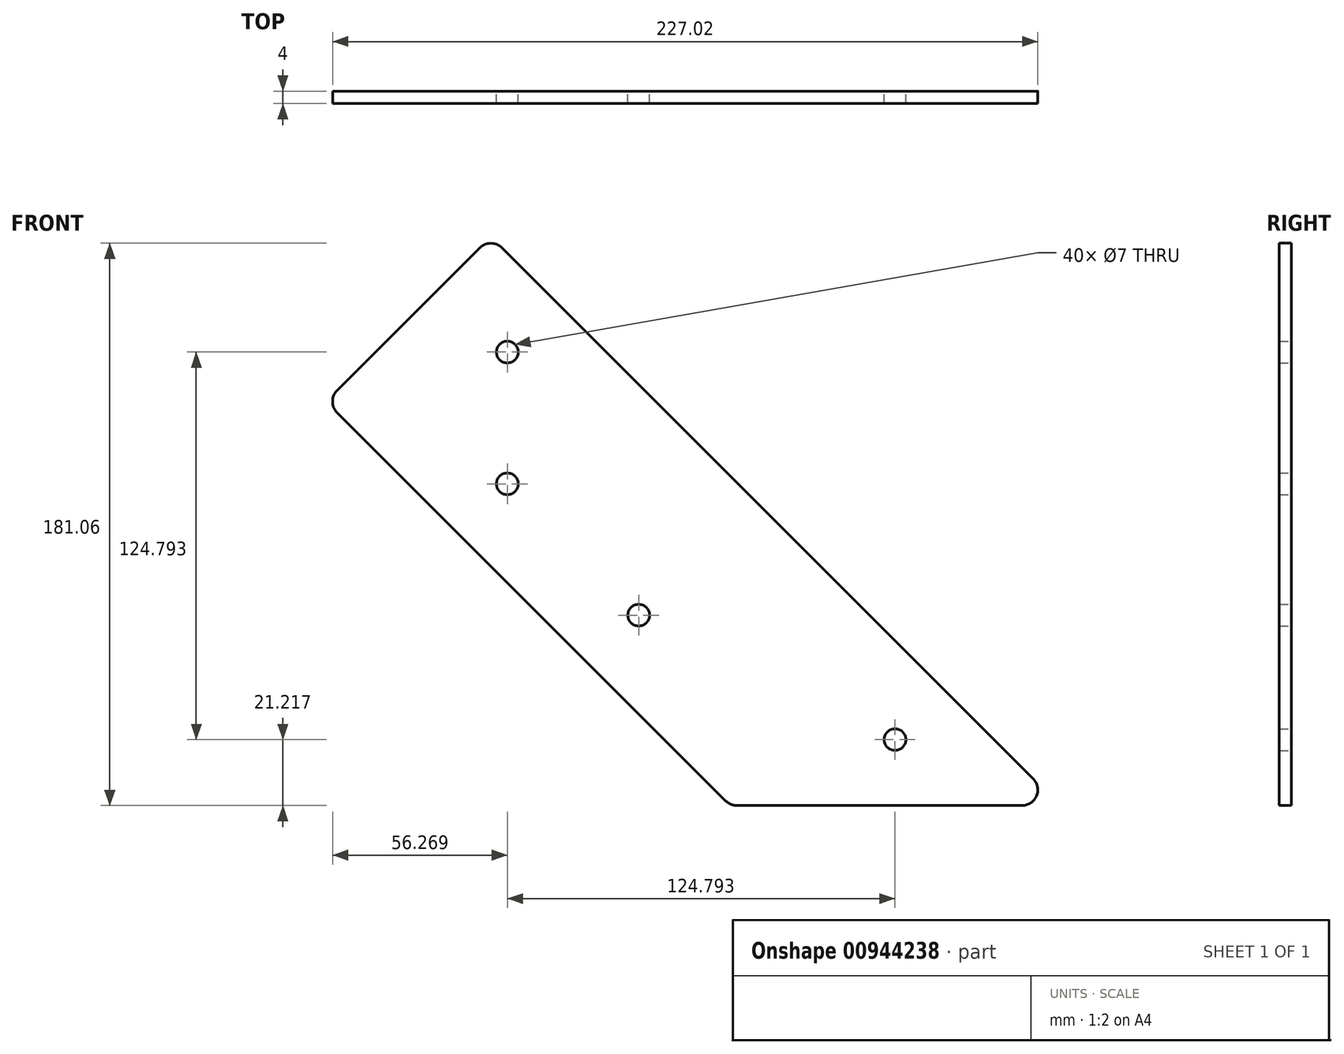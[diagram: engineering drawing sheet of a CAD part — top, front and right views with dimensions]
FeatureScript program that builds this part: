
annotation { "Feature Type Name" : "Feature", "Feature Type Description" : "" }
export const myFeature = defineFeature(function(context is Context, id is Id, definition is map)
    precondition{}
    {
        {
            var Q0;
            Q0=qCreatedBy(makeId("Front.planeOp"),FACE);
            var sketch = newSketch(context, id + "F0", { "sketchPlane" : qUnion([Q0])});
            skLineSegment(sketch, "E0.0", {"start": v(124.61, -80.69) * mm, "end": v(32.69, -80.69) * mm});
            skLineSegment(sketch, "E0.2", {"start": v(29.15, -79.22) * mm, "end": v(-57.05, 6.98) * mm});
            skCircle(sketch, "E1", {"center": v(1.15, -19.4) * mm, "radius": 3.5 * mm});
            skCircle(sketch, "E2", {"center": v(83.65, -59.47) * mm, "radius": 3.5 * mm});
            skCircle(sketch, "E3", {"center": v(-41.14, 22.9) * mm, "radius": 3.5 * mm});
            skCircle(sketch, "E4", {"center": v(-41.14, 65.32) * mm, "radius": 3.5 * mm});
            skPoint(sketch, "E5.visualSharp", {"position": v(30.62, -80.69) * mm});
            skArc(sketch, "E5.filletArc", {"start": v(29.15, -79.22) * mm, "mid": v(30.78, -80.3) * mm, "end": v(32.69, -80.69) * mm});
            skPoint(sketch, "E6.visualSharp", {"position": v(136.68, -80.69) * mm});
            skArc(sketch, "E6.filletArc", {"start": v(124.61, -80.69) * mm, "mid": v(129.23, -77.6) * mm, "end": v(128.15, -72.15) * mm});
            skLineSegment(sketch, "E7", {"start": v(-57.05, 6.98) * mm, "end": v(-95.94, 45.87) * mm});
            skLineSegment(sketch, "E8", {"start": v(-95.94, 52.95) * mm, "end": v(-49.98, 98.9) * mm});
            skPoint(sketch, "E9.visualSharp", {"position": v(-99.48, 49.41) * mm});
            skArc(sketch, "E9.filletArc", {"start": v(-95.94, 52.95) * mm, "mid": v(-97.4, 49.41) * mm, "end": v(-95.94, 45.87) * mm});
            skLineSegment(sketch, "E10", {"start": v(-42.9, 98.9) * mm, "end": v(128.15, -72.15) * mm});
            skPoint(sketch, "E11.visualSharp", {"position": v(-46.44, 102.44) * mm});
            skArc(sketch, "E11.filletArc", {"start": v(-42.9, 98.9) * mm, "mid": v(-46.44, 100.37) * mm, "end": v(-49.98, 98.9) * mm});
            skSolve(sketch);
        }
        {
            var Q0;
            Q0=makeQuery(id+"F0.imprint","IMPRINT",FACE,{"disambiguationData":[TD([[makeQuery(id+"F0.imprint","IMPRINT",EDGE,{"derivedFrom":sQuery(id+"F0.wireOp",EDGE,"E0.0")}),-1.0]])]});
            extrude(context, id + "F1", {"entities" : qUnion([Q0]), "depth" : 4 * mm, "offsetDistance" : 25 * mm});
        }
    });
